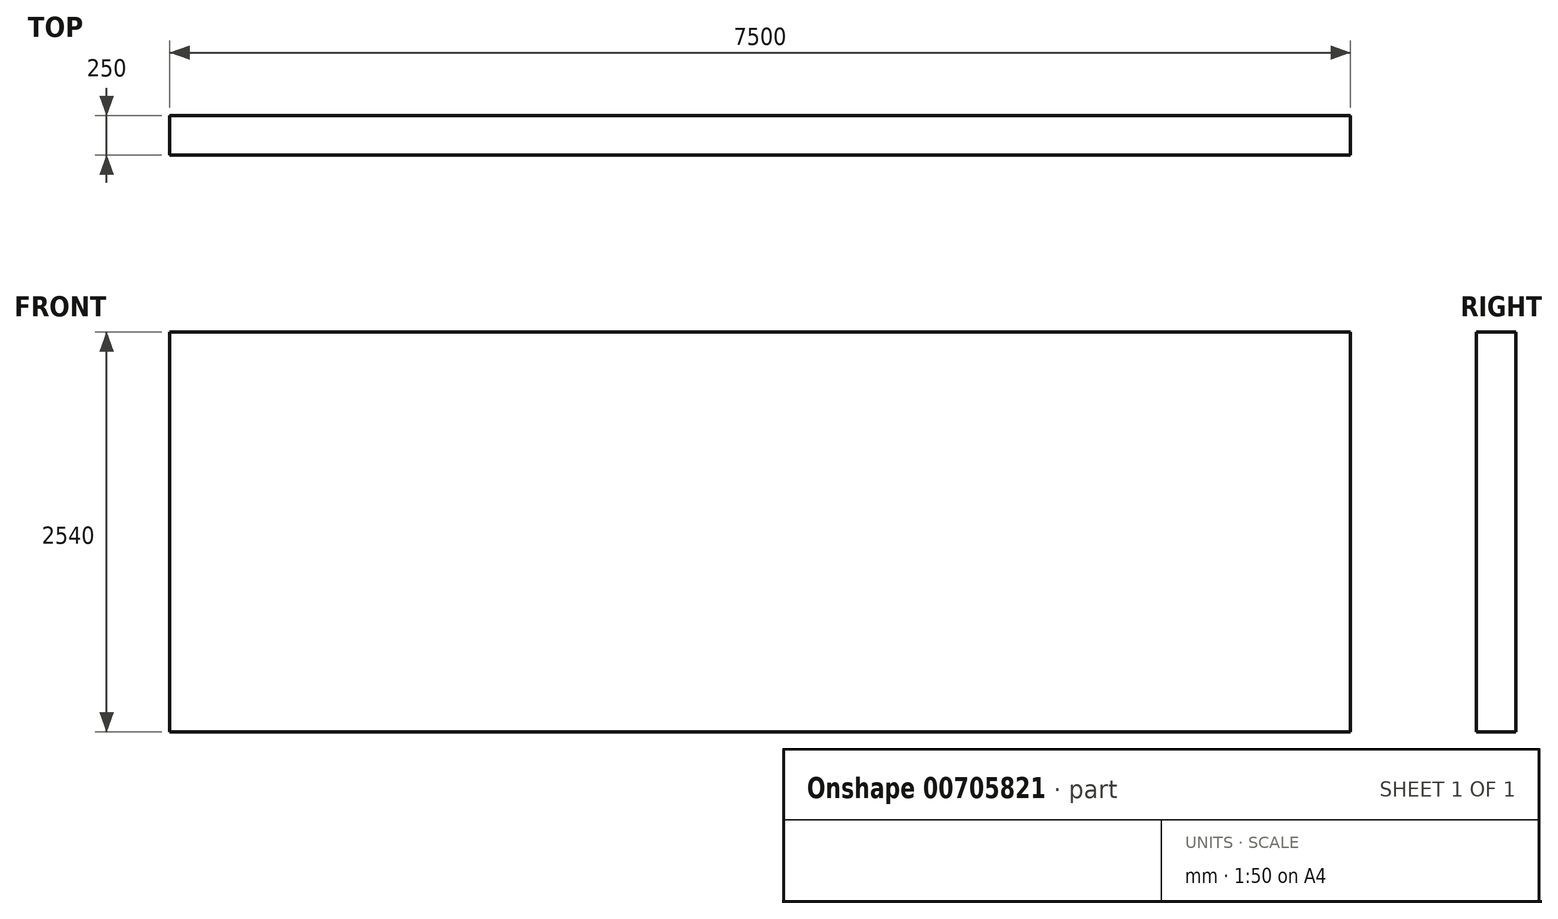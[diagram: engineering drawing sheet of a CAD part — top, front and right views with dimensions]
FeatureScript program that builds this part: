
annotation { "Feature Type Name" : "Feature", "Feature Type Description" : "" }
export const myFeature = defineFeature(function(context is Context, id is Id, definition is map)
    precondition{}
    {
        {
            var Q0;
            Q0=qCreatedBy(makeId("Top.planeOp"),FACE);
            var sketch = newSketch(context, id + "F0", { "sketchPlane" : qUnion([Q0])});
            skLineSegment(sketch, "E0.bottom", {"start": v(-81.81, -13.52) * mm, "end": v(7418.19, -13.52) * mm});
            skLineSegment(sketch, "E0.top", {"start": v(-81.81, 236.48) * mm, "end": v(7418.19, 236.48) * mm});
            skLineSegment(sketch, "E0.left", {"start": v(-81.81, -13.52) * mm, "end": v(-81.81, 236.48) * mm});
            skLineSegment(sketch, "E0.right", {"start": v(7418.19, -13.52) * mm, "end": v(7418.19, 236.48) * mm});
            skSolve(sketch);
        }
        {
            var Q0;
            Q0=makeQuery(id+"F0.imprint","IMPRINT",FACE,{"disambiguationData":[TD([[makeQuery(id+"F0.imprint","IMPRINT",EDGE,{"derivedFrom":sQuery(id+"F0.wireOp",EDGE,"E0.bottom")}),1.0]])]});
            extrude(context, id + "F1", {"entities" : qUnion([Q0]), "depth" : 2540 * mm, "offsetDistance" : 25 * mm});
        }
    });
